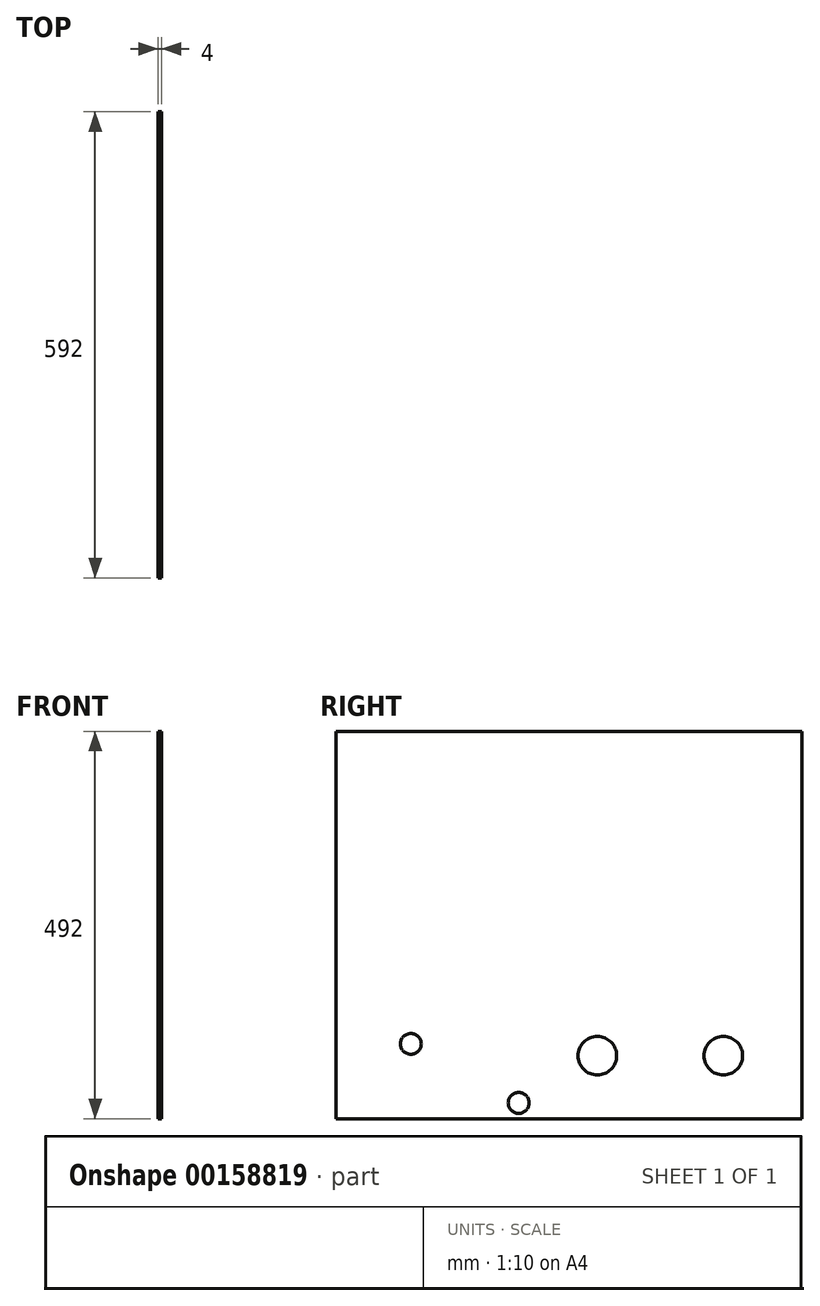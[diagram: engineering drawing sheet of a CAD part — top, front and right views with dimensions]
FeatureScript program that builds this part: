
annotation { "Feature Type Name" : "Feature", "Feature Type Description" : "" }
export const myFeature = defineFeature(function(context is Context, id is Id, definition is map)
    precondition{}
    {
        {
            var Q0;
            Q0=qCreatedBy(makeId("Right.planeOp"),FACE);
            var sketch = newSketch(context, id + "F0", { "sketchPlane" : qUnion([Q0])});
            skLineSegment(sketch, "E0.0", {"start": v(-8, 492) * mm, "end": v(592, 492) * mm});
            skLineSegment(sketch, "E1.bottom", {"start": v(0, 0) * mm, "end": v(592, 0) * mm});
            skLineSegment(sketch, "E1.top", {"start": v(0, 492) * mm, "end": v(592, 492) * mm});
            skLineSegment(sketch, "E1.left", {"start": v(0, 0) * mm, "end": v(0, 492) * mm});
            skLineSegment(sketch, "E1.right", {"start": v(592, 0) * mm, "end": v(592, 492) * mm});
            skPoint(sketch, "E2.0", {"position": v(492, 80) * mm});
            skPoint(sketch, "E3.0", {"position": v(332, 80) * mm});
            skCircle(sketch, "E4.0", {"center": v(95, 95) * mm, "radius": 13.25 * mm});
            skCircle(sketch, "E5", {"center": v(492, 80) * mm, "radius": 24.5 * mm});
            skCircle(sketch, "E6", {"center": v(332, 80) * mm, "radius": 24.5 * mm});
            skCircle(sketch, "E7", {"center": v(232, 20) * mm, "radius": 13.25 * mm});
            skSolve(sketch);
        }
        {
            var Q0;
            Q0 = qSketchRegion(id + "F0", true);
            extrude(context, id + "F1", {"entities" : qUnion([Q0]), "depth" : 4 * mm});
        }
    });
